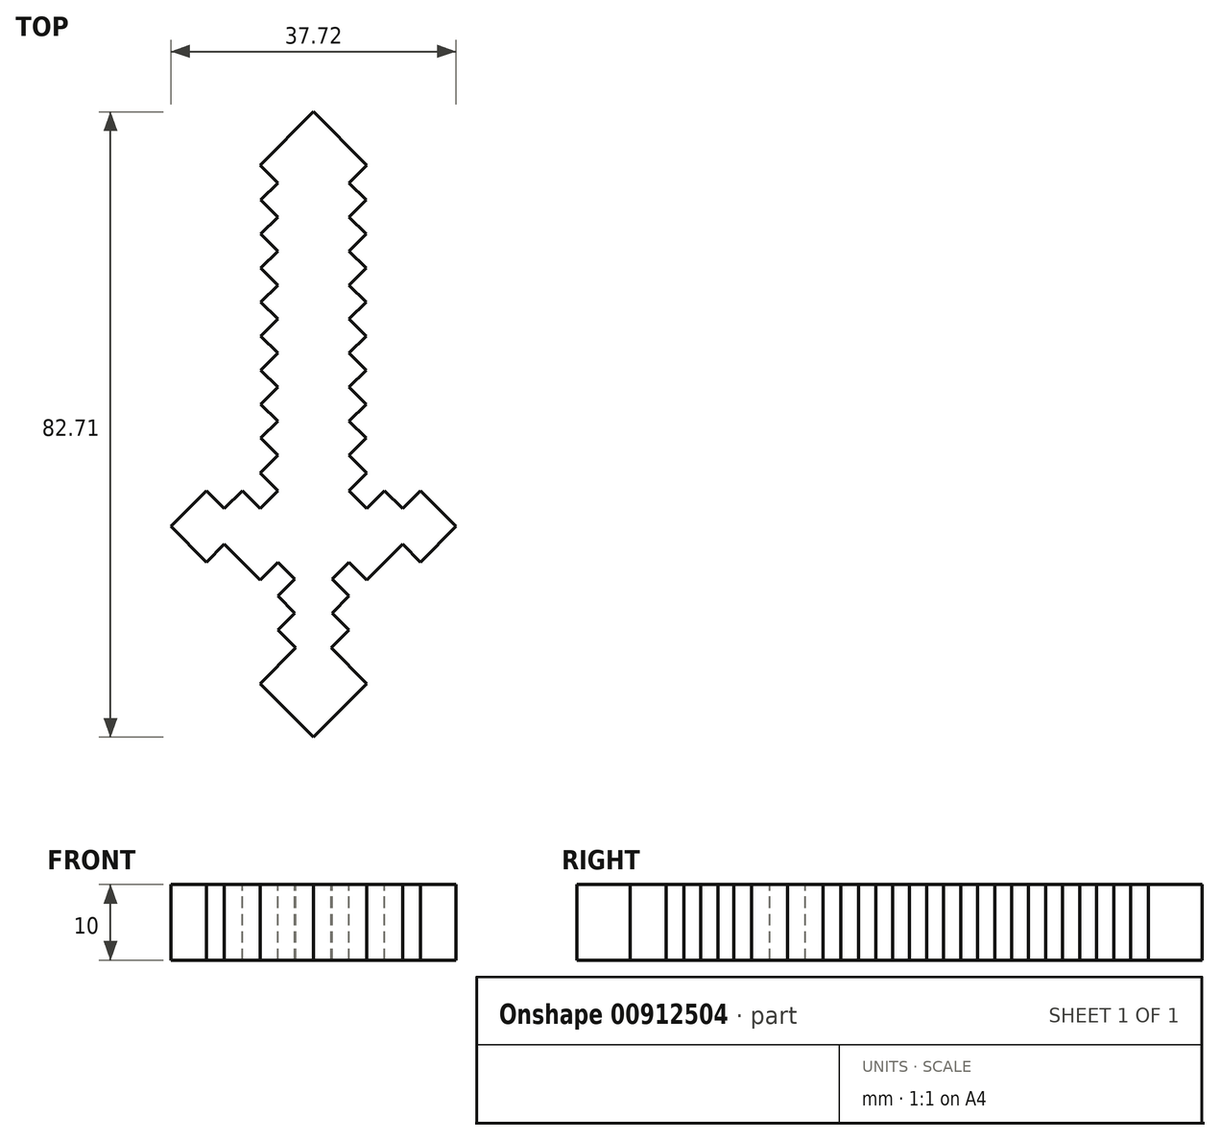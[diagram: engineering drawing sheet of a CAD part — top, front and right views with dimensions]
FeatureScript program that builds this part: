
annotation { "Feature Type Name" : "Feature", "Feature Type Description" : "" }
export const myFeature = defineFeature(function(context is Context, id is Id, definition is map)
    precondition{}
    {
        {
            var Q0;
            Q0=qCreatedBy(makeId("Top.planeOp"),FACE);
            var sketch = newSketch(context, id + "F0", { "sketchPlane" : qUnion([Q0])});
            skLineSegment(sketch, "E0.bottom", {"start": v(20, 50) * mm, "end": v(-20, 50) * mm});
            skLineSegment(sketch, "E0.top", {"start": v(20, -50) * mm, "end": v(-20, -50) * mm});
            skLineSegment(sketch, "E0.left", {"start": v(20, 50) * mm, "end": v(20, -50) * mm});
            skLineSegment(sketch, "E0.right", {"start": v(-20, 50) * mm, "end": v(-20, -50) * mm});
            skPoint(sketch, "E0.middle", {"position": v(0, 0) * mm});
            skSolve(sketch);
        }
        {
            var Q0;
            Q0=makeQuery(id+"F0.imprint","IMPRINT",FACE,{"disambiguationData":[TD([[makeQuery(id+"F0.imprint","IMPRINT",EDGE,{"derivedFrom":sQuery(id+"F0.wireOp",EDGE,"E0.bottom")}),1.0]])]});
            extrude(context, id + "F1", {"entities" : qUnion([Q0]), "depth" : 15 * mm, "offsetDistance" : 25 * mm});
        }
        {
            var Q0;
            Q0=makeQuery(id+"F1.opExtrude","CAP_FACE",FACE,{"disambiguationData":[OSD([sQuery(id+"F0.wireOp",EDGE,"E0.bottom"),sQuery(id+"F0.wireOp",EDGE,"E0.top"),sQuery(id+"F0.wireOp",EDGE,"E0.left"),sQuery(id+"F0.wireOp",EDGE,"E0.right")])],"isStart":true});
            var sketch = newSketch(context, id + "F2", { "sketchPlane" : qUnion([Q0])});
            skLineSegment(sketch, "E1", {"start": v(0, 50) * mm, "end": v(7.07, 42.93) * mm});
            skLineSegment(sketch, "E2.0.0", {"start": v(20, 50) * mm, "end": v(-20, 50) * mm});
            skLineSegment(sketch, "E2.0.1", {"start": v(-20, 50) * mm, "end": v(-20, -50) * mm});
            skLineSegment(sketch, "E2.0.2", {"start": v(-20, -50) * mm, "end": v(20, -50) * mm});
            skLineSegment(sketch, "E2.0.3", {"start": v(20, -50) * mm, "end": v(20, 50) * mm});
            skLineSegment(sketch, "E3", {"start": v(0, 50) * mm, "end": v(-7.07, 42.93) * mm});
            skLineSegment(sketch, "E4", {"start": v(-7.07, 42.93) * mm, "end": v(-2.36, 38.21) * mm});
            skLineSegment(sketch, "E5", {"start": v(2.36, 38.21) * mm, "end": v(4.71, 35.86) * mm});
            skLineSegment(sketch, "E6", {"start": v(4.71, 35.86) * mm, "end": v(2.46, 33.6) * mm});
            skLineSegment(sketch, "E7", {"start": v(-4.71, 35.86) * mm, "end": v(-2.36, 38.21) * mm});
            skLineSegment(sketch, "E8.0.1.0", {"start": v(4.71, 31.36) * mm, "end": v(2.46, 29.1) * mm});
            skLineSegment(sketch, "E8.0.1.1", {"start": v(-2.46, 29.1) * mm, "end": v(-4.71, 31.36) * mm});
            skLineSegment(sketch, "E8.0.1.2", {"start": v(-4.71, 31.36) * mm, "end": v(-2.36, 33.71) * mm});
            skLineSegment(sketch, "E8.direction1", {"start": v(4.5, 31.14) * mm, "end": v(27, 31.14) * mm, "construction": true});
            skLineSegment(sketch, "E8.direction2", {"start": v(0, 31.14) * mm, "end": v(0, 26.64) * mm, "construction": true});
            skLineSegment(sketch, "E9.0.1.0", {"start": v(4.71, 26.86) * mm, "end": v(4.5, 26.64) * mm});
            skLineSegment(sketch, "E9.0.1.2", {"start": v(-4.71, 26.86) * mm, "end": v(-2.46, 29.1) * mm});
            skLineSegment(sketch, "E9.direction1", {"start": v(0, 26.64) * mm, "end": v(25, 26.64) * mm, "construction": true});
            skLineSegment(sketch, "E9.direction2", {"start": v(0, 26.64) * mm, "end": v(0, 22.14) * mm, "construction": true});
            skLineSegment(sketch, "E10", {"start": v(4.71, 26.86) * mm, "end": v(7.07, 29.21) * mm});
            skLineSegment(sketch, "E11", {"start": v(-4.71, 26.86) * mm, "end": v(-7.07, 29.21) * mm});
            skLineSegment(sketch, "E12", {"start": v(7.07, 29.21) * mm, "end": v(11.79, 24.5) * mm});
            skLineSegment(sketch, "E13", {"start": v(-7.07, 29.21) * mm, "end": v(-11.79, 24.5) * mm});
            skLineSegment(sketch, "E14", {"start": v(11.79, 24.5) * mm, "end": v(14.14, 26.86) * mm});
            skLineSegment(sketch, "E15", {"start": v(14.14, 26.86) * mm, "end": v(18.86, 22.14) * mm});
            skLineSegment(sketch, "E16", {"start": v(18.86, 22.14) * mm, "end": v(14.14, 17.43) * mm});
            skLineSegment(sketch, "E17", {"start": v(14.14, 17.43) * mm, "end": v(11.79, 19.79) * mm});
            skLineSegment(sketch, "E18", {"start": v(11.79, 19.79) * mm, "end": v(9.43, 17.43) * mm});
            skLineSegment(sketch, "E19", {"start": v(9.43, 17.43) * mm, "end": v(7.07, 19.79) * mm});
            skLineSegment(sketch, "E20", {"start": v(7.07, 19.79) * mm, "end": v(4.71, 17.43) * mm});
            skLineSegment(sketch, "E21", {"start": v(4.71, 17.43) * mm, "end": v(7.07, 15.07) * mm});
            skLineSegment(sketch, "E22", {"start": v(7.07, 15.07) * mm, "end": v(4.71, 12.72) * mm});
            skLineSegment(sketch, "E23", {"start": v(4.71, 12.72) * mm, "end": v(7.07, 10.36) * mm});
            skLineSegment(sketch, "E24.0.1.0", {"start": v(4.71, 8.22) * mm, "end": v(7.07, 5.86) * mm});
            skLineSegment(sketch, "E24.0.1.1", {"start": v(7.07, 10.57) * mm, "end": v(4.71, 8.22) * mm});
            skLineSegment(sketch, "E24.0.2.0", {"start": v(4.71, 3.72) * mm, "end": v(7.07, 1.36) * mm});
            skLineSegment(sketch, "E24.0.2.1", {"start": v(7.07, 6.07) * mm, "end": v(4.71, 3.72) * mm});
            skLineSegment(sketch, "E24.0.3.0", {"start": v(4.71, -0.78) * mm, "end": v(7.07, -3.14) * mm});
            skLineSegment(sketch, "E24.0.3.1", {"start": v(7.07, 1.57) * mm, "end": v(4.71, -0.78) * mm});
            skLineSegment(sketch, "E24.0.4.0", {"start": v(4.71, -5.28) * mm, "end": v(7.07, -7.64) * mm});
            skLineSegment(sketch, "E24.0.4.1", {"start": v(7.07, -2.93) * mm, "end": v(4.71, -5.28) * mm});
            skLineSegment(sketch, "E24.0.5.0", {"start": v(4.71, -9.78) * mm, "end": v(7.07, -12.14) * mm});
            skLineSegment(sketch, "E24.0.5.1", {"start": v(7.07, -7.43) * mm, "end": v(4.71, -9.78) * mm});
            skLineSegment(sketch, "E24.direction1", {"start": v(7.07, 10.36) * mm, "end": v(32.07, 10.36) * mm, "construction": true});
            skLineSegment(sketch, "E25.MirrorCS", {"start": v(-7.07, 19.79) * mm, "end": v(-4.71, 17.43) * mm});
            skLineSegment(sketch, "E26.MirrorCS", {"start": v(-4.71, 17.43) * mm, "end": v(-7.07, 15.07) * mm});
            skLineSegment(sketch, "E27.MirrorCS", {"start": v(-7.07, 15.07) * mm, "end": v(-4.71, 12.72) * mm});
            skLineSegment(sketch, "E28.MirrorCS", {"start": v(-7.07, -2.93) * mm, "end": v(-4.71, -5.28) * mm});
            skLineSegment(sketch, "E29.MirrorCS", {"start": v(-7.07, 6.07) * mm, "end": v(-4.71, 3.72) * mm});
            skLineSegment(sketch, "E30.MirrorCS", {"start": v(-9.43, 17.43) * mm, "end": v(-7.07, 19.79) * mm});
            skLineSegment(sketch, "E31.MirrorCS", {"start": v(-4.71, 12.72) * mm, "end": v(-7.07, 10.36) * mm});
            skLineSegment(sketch, "E32.MirrorCS", {"start": v(-4.71, -9.78) * mm, "end": v(-7.07, -12.14) * mm});
            skLineSegment(sketch, "E33.MirrorCS", {"start": v(-4.71, -0.78) * mm, "end": v(-7.07, -3.14) * mm});
            skLineSegment(sketch, "E34.MirrorCS", {"start": v(-4.71, 8.22) * mm, "end": v(-7.07, 5.86) * mm});
            skLineSegment(sketch, "E35.MirrorCS", {"start": v(-7.07, 10.57) * mm, "end": v(-4.71, 8.22) * mm});
            skLineSegment(sketch, "E36.MirrorCS", {"start": v(-7.07, 1.57) * mm, "end": v(-4.71, -0.78) * mm});
            skLineSegment(sketch, "E37.MirrorCS", {"start": v(-4.71, 3.72) * mm, "end": v(-7.07, 1.36) * mm});
            skLineSegment(sketch, "E38.MirrorCS", {"start": v(-4.71, 35.86) * mm, "end": v(-2.46, 33.6) * mm});
            skLineSegment(sketch, "E39.MirrorCS", {"start": v(-11.79, 19.79) * mm, "end": v(-9.43, 17.43) * mm});
            skLineSegment(sketch, "E40.MirrorCS", {"start": v(-4.71, -5.28) * mm, "end": v(-7.07, -7.64) * mm});
            skLineSegment(sketch, "E41.MirrorCS", {"start": v(-7.07, -7.43) * mm, "end": v(-4.71, -9.78) * mm});
            skLineSegment(sketch, "E42.MirrorCS", {"start": v(-4.71, 31.36) * mm, "end": v(-2.46, 29.1) * mm});
            skLineSegment(sketch, "E43.MirrorCS", {"start": v(-11.79, 24.5) * mm, "end": v(-14.14, 26.86) * mm});
            skLineSegment(sketch, "E44.MirrorCS", {"start": v(-14.14, 17.43) * mm, "end": v(-11.79, 19.79) * mm});
            skLineSegment(sketch, "E45.MirrorCS", {"start": v(-18.86, 22.14) * mm, "end": v(-14.14, 17.43) * mm});
            skLineSegment(sketch, "E46.MirrorCS", {"start": v(-14.14, 26.86) * mm, "end": v(-18.86, 22.14) * mm});
            skLineSegment(sketch, "E47.0.1.0", {"start": v(7.07, -11.93) * mm, "end": v(4.71, -14.28) * mm});
            skLineSegment(sketch, "E47.0.1.1", {"start": v(4.71, -14.28) * mm, "end": v(7.07, -16.64) * mm});
            skLineSegment(sketch, "E47.0.1.2", {"start": v(-20, 45.5) * mm, "end": v(-20, -54.5) * mm});
            skLineSegment(sketch, "E47.0.2.0", {"start": v(7.07, -16.43) * mm, "end": v(4.71, -18.78) * mm});
            skLineSegment(sketch, "E47.0.2.1", {"start": v(4.71, -18.78) * mm, "end": v(7.07, -21.14) * mm});
            skLineSegment(sketch, "E47.0.2.2", {"start": v(-20, 41) * mm, "end": v(-20, -59) * mm});
            skLineSegment(sketch, "E47.0.3.0", {"start": v(7.07, -20.93) * mm, "end": v(4.71, -23.28) * mm});
            skLineSegment(sketch, "E47.0.3.1", {"start": v(4.71, -23.28) * mm, "end": v(7.07, -25.64) * mm});
            skLineSegment(sketch, "E47.0.3.2", {"start": v(-20, 36.5) * mm, "end": v(-20, -63.5) * mm});
            skLineSegment(sketch, "E47.direction1", {"start": v(4.71, -9.78) * mm, "end": v(29.71, -9.78) * mm, "construction": true});
            skLineSegment(sketch, "E47.direction2", {"start": v(4.71, -9.78) * mm, "end": v(4.71, -14.28) * mm, "construction": true});
            skLineSegment(sketch, "E48", {"start": v(7.07, -25.64) * mm, "end": v(0, -32.71) * mm});
            skLineSegment(sketch, "E49.MirrorCS", {"start": v(-7.07, -25.64) * mm, "end": v(0, -32.71) * mm});
            skLineSegment(sketch, "E50.MirrorCS", {"start": v(-4.71, -23.28) * mm, "end": v(-7.07, -25.64) * mm});
            skLineSegment(sketch, "E51.MirrorCS", {"start": v(-7.07, -20.93) * mm, "end": v(-4.71, -23.28) * mm});
            skLineSegment(sketch, "E52.MirrorCS", {"start": v(-7.07, -16.43) * mm, "end": v(-4.71, -18.78) * mm});
            skLineSegment(sketch, "E53.MirrorCS", {"start": v(-4.71, -18.78) * mm, "end": v(-7.07, -21.14) * mm});
            skLineSegment(sketch, "E54.MirrorCS", {"start": v(-4.71, -14.28) * mm, "end": v(-7.07, -16.64) * mm});
            skLineSegment(sketch, "E55.MirrorCS", {"start": v(-7.07, -11.93) * mm, "end": v(-4.71, -14.28) * mm});
            skPoint(sketch, "E56.start.orphan", {"position": v(0, 40.57) * mm});
            skPoint(sketch, "E57.orphan", {"position": v(-2.36, 38.21) * mm});
            skLineSegment(sketch, "E58.trimOffspring", {"start": v(2.36, 33.71) * mm, "end": v(4.71, 31.36) * mm});
            skLineSegment(sketch, "E59.trimOffspring", {"start": v(2.46, 29.1) * mm, "end": v(4.71, 26.86) * mm});
            skLineSegment(sketch, "E60.trimOffspring", {"start": v(-2.46, 29.1) * mm, "end": v(-4.71, 26.86) * mm});
            skLineSegment(sketch, "E61.trimOffspring", {"start": v(-2.46, 33.6) * mm, "end": v(-4.71, 35.86) * mm});
            skLineSegment(sketch, "E62.trimOffspring", {"start": v(-2.36, 33.71) * mm, "end": v(-4.71, 31.36) * mm});
            skPoint(sketch, "E63.orphan", {"position": v(2.36, 38.21) * mm});
            skLineSegment(sketch, "E64.trimOffspring", {"start": v(2.36, 38.21) * mm, "end": v(7.07, 42.93) * mm});
            skPoint(sketch, "E65.start.orphan", {"position": v(9.43, 22.14) * mm});
            skSolve(sketch);
        }
        {
            var Q0;
            Q0=makeQuery(id+"F2.imprint","IMPRINT",FACE,{"disambiguationData":[TD([[makeQuery(id+"F2.imprint","IMPRINT",EDGE,{"derivedFrom":sQuery(id+"F2.wireOp",EDGE,"E1")}),-1.0]])]});
            extrude(context, id + "F3", {"entities" : qUnion([Q0]), "operationType" : NewBodyOperationType.ADD, "depth" : 10 * mm, "offsetDistance" : 25 * mm});
        }
        {
            var Q0;
            Q0=makeQuery(id+"F1.opExtrude","SWEPT_FACE",FACE,{"disambiguationData":[OSD([sQuery(id+"F0.wireOp",EDGE,"E0.right")])]});
            var sketch = newSketch(context, id + "F4", { "sketchPlane" : qUnion([Q0])});
            skLineSegment(sketch, "E66.0.0", {"start": v(-50, 0) * mm, "end": v(50, 0) * mm});
            skLineSegment(sketch, "E66.0.1", {"start": v(50, 0) * mm, "end": v(50, 15) * mm});
            skLineSegment(sketch, "E66.0.2", {"start": v(50, 15) * mm, "end": v(-50, 15) * mm});
            skLineSegment(sketch, "E66.0.3", {"start": v(-50, 15) * mm, "end": v(-50, 0) * mm});
            skSolve(sketch);
        }
        {
            var Q0;
            Q0 = qSketchRegion(id + "F4", true);
            extrude(context, id + "F5", {"entities" : qUnion([Q0]), "operationType" : NewBodyOperationType.REMOVE, "oppositeDirection" : true, "depth" : 100 * mm, "offsetDistance" : 25 * mm});
        }
    });
